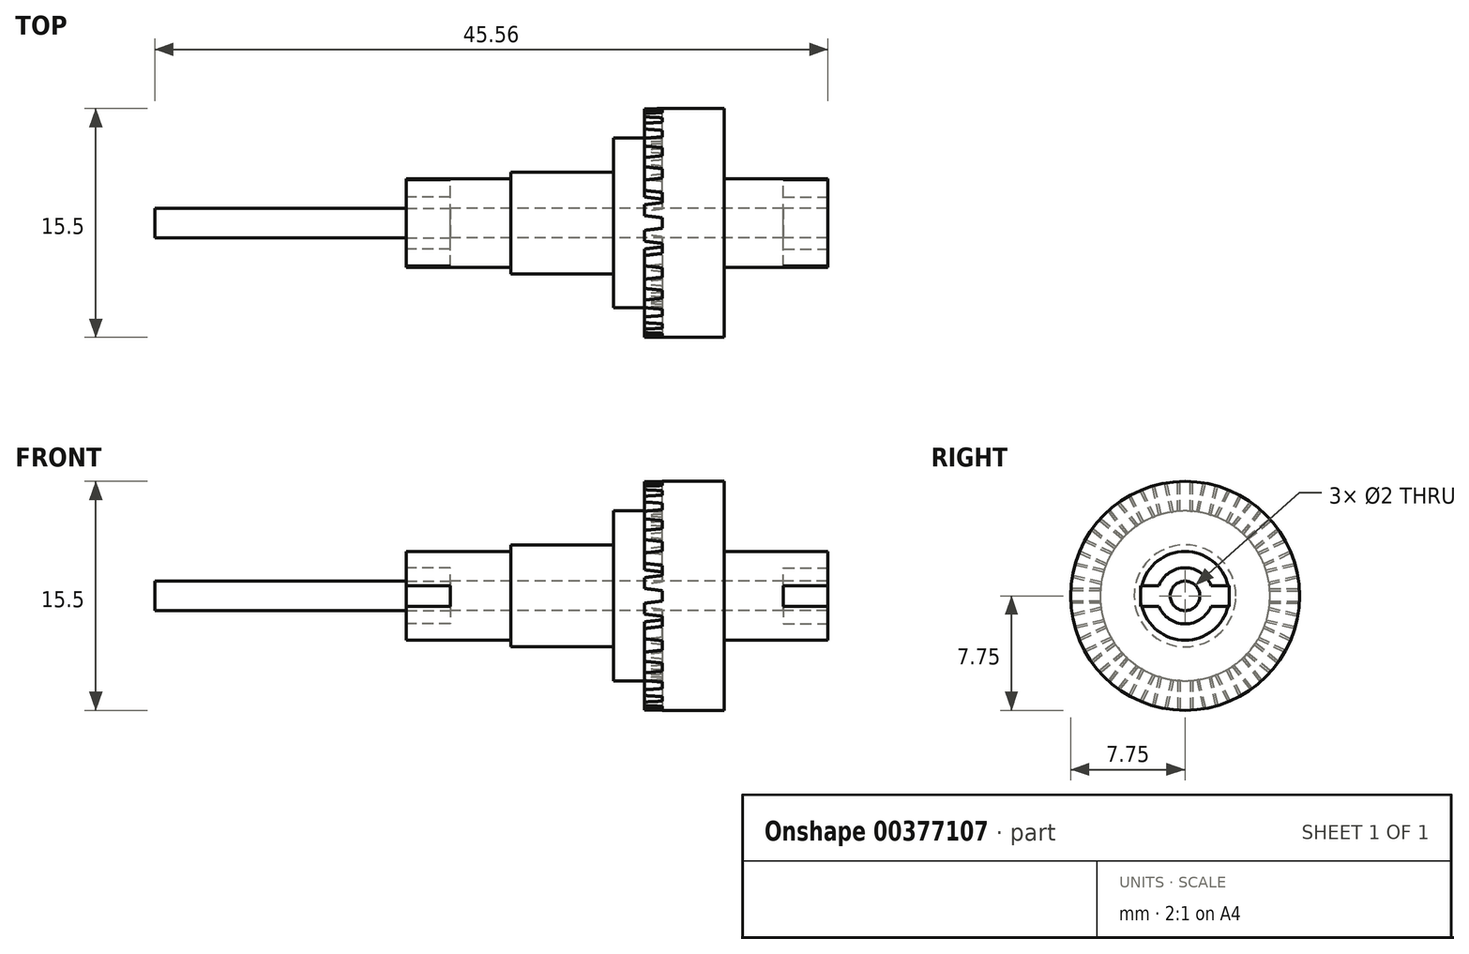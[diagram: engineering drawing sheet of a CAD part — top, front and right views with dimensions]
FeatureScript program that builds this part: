
annotation { "Feature Type Name" : "Feature", "Feature Type Description" : "" }
export const myFeature = defineFeature(function(context is Context, id is Id, definition is map)
    precondition{}
    {
        {
            var Q0;
            Q0=qCreatedBy(makeId("Top.planeOp"),FACE);
            var sketch = newSketch(context, id + "F0", { "sketchPlane" : qUnion([Q0])});
            skLineSegment(sketch, "E0", {"start": v(14.28, 0) * mm, "end": v(-14.28, 0) * mm});
            skLineSegment(sketch, "E1", {"start": v(14.28, 0) * mm, "end": v(14.28, -3) * mm});
            skLineSegment(sketch, "E2", {"start": v(14.28, -3) * mm, "end": v(7.28, -3) * mm});
            skLineSegment(sketch, "E3", {"start": v(7.28, -3) * mm, "end": v(7.28, -7.75) * mm});
            skLineSegment(sketch, "E4", {"start": v(7.28, -7.75) * mm, "end": v(1.88, -7.75) * mm});
            skLineSegment(sketch, "E5", {"start": v(1.88, -7.75) * mm, "end": v(1.88, -5.75) * mm});
            skLineSegment(sketch, "E6", {"start": v(1.88, -5.75) * mm, "end": v(-0.22, -5.75) * mm});
            skLineSegment(sketch, "E7", {"start": v(-0.22, -5.75) * mm, "end": v(-0.22, -3.45) * mm});
            skLineSegment(sketch, "E8", {"start": v(-0.22, -3.45) * mm, "end": v(-7.18, -3.45) * mm});
            skLineSegment(sketch, "E9", {"start": v(-7.18, -3.45) * mm, "end": v(-7.18, -3) * mm});
            skLineSegment(sketch, "E10", {"start": v(-7.18, -3) * mm, "end": v(-14.28, -3) * mm});
            skLineSegment(sketch, "E11", {"start": v(-14.28, -3) * mm, "end": v(-14.28, 0) * mm});
            skLineSegment(sketch, "E12.MirrorCS", {"start": v(-7.18, 3.45) * mm, "end": v(-7.18, 3) * mm, "construction": true});
            skLineSegment(sketch, "E13.MirrorCS", {"start": v(1.88, 5.75) * mm, "end": v(-0.22, 5.75) * mm, "construction": true});
            skLineSegment(sketch, "E14.MirrorCS", {"start": v(1.88, 7.75) * mm, "end": v(1.88, 5.75) * mm, "construction": true});
            skLineSegment(sketch, "E15.MirrorCS", {"start": v(-7.18, 3) * mm, "end": v(-14.28, 3) * mm, "construction": true});
            skLineSegment(sketch, "E16.MirrorCS", {"start": v(14.28, 3) * mm, "end": v(7.28, 3) * mm, "construction": true});
            skLineSegment(sketch, "E17.MirrorCS", {"start": v(7.28, 3) * mm, "end": v(7.28, 7.75) * mm, "construction": true});
            skLineSegment(sketch, "E18.MirrorCS", {"start": v(7.28, 7.75) * mm, "end": v(1.87, 7.75) * mm, "construction": true});
            skLineSegment(sketch, "E19.MirrorCS", {"start": v(-0.22, 5.75) * mm, "end": v(-0.22, 3.45) * mm, "construction": true});
            skLineSegment(sketch, "E20.MirrorCS", {"start": v(-0.22, 3.45) * mm, "end": v(-7.18, 3.45) * mm, "construction": true});
            skLineSegment(sketch, "E21.MirrorCS", {"start": v(-14.28, 3) * mm, "end": v(-14.28, 0) * mm, "construction": true});
            skLineSegment(sketch, "E22.MirrorCS", {"start": v(14.28, 0) * mm, "end": v(14.28, 3) * mm, "construction": true});
            skLineSegment(sketch, "E23", {"start": v(-11.43, 3) * mm, "end": v(-11.43, -3) * mm, "construction": true});
            skSolve(sketch);
        }
        {
            var Q0;
            Q0 = qSketchRegion(id + "F0", true);
            var Q1;
            Q1=sQuery(id+"F0.wireOp",EDGE,"E0");
            revolve(context, id + "F1", {"entities" : qUnion([Q0]), "axis" : qUnion([Q1]), "revolveType" : RevolveType.FULL});
        }
        {
            var Q0;
            Q0=qCreatedBy(makeId("Right.planeOp"),FACE);
            var sketch = newSketch(context, id + "F2", { "sketchPlane" : qUnion([Q0])});
            skLineSegment(sketch, "E24", {"start": v(0, 0) * mm, "end": v(0, 7.75) * mm, "construction": true});
            skSolve(sketch);
        }
        {
            var Q0;
            Q0=qCreatedBy(makeId("Top.planeOp"),FACE);
            var Q1;
            Q1=sQuery(id+"F2.wireOp",VERTEX,"E24.end");
            cPlane(context, id + "F3", {"entities" : qUnion([Q0, Q1]), "cplaneType" : CPlaneType.PLANE_POINT, "offset" : 25 * mm, "width" : 150 * mm, "height" : 150 * mm});
        }
        {
            var Q0;
            Q0=qCreatedBy(id+"F3.planeOp",FACE);
            var sketch = newSketch(context, id + "F4", { "sketchPlane" : qUnion([Q0])});
            skLineSegment(sketch, "E25", {"start": v(1.88, 0.5) * mm, "end": v(1.88, -0.5) * mm});
            skPoint(sketch, "E26", {"position": v(1.88, 0) * mm});
            skLineSegment(sketch, "E27", {"start": v(3.08, 0.35) * mm, "end": v(3.08, -0.35) * mm});
            skPoint(sketch, "E28", {"position": v(3.08, 0) * mm});
            skLineSegment(sketch, "E29", {"start": v(1.88, 0.5) * mm, "end": v(3.08, 0.35) * mm});
            skLineSegment(sketch, "E30", {"start": v(1.88, -0.5) * mm, "end": v(3.08, -0.35) * mm});
            skSolve(sketch);
        }
        {
            var Q0;
            Q0 = qSketchRegion(id + "F4", true);
            var Q1;
            Q1=makeQuery(id+"F1.opRevolve","SWEPT_FACE",FACE,{"disambiguationData":[OSD([sQuery(id+"F0.wireOp",EDGE,"E6")])]});
            extrude(context, id + "F5", {"entities" : qUnion([Q0]), "endBound" : BoundingType.UP_TO_SURFACE, "oppositeDirection" : true, "endBoundEntityFace" : qUnion([Q1]), "depth" : 25 * mm});
        }
        {
            var Q0;
            Q0=makeQuery(id+"F5.opExtrude","SWEPT_BODY",BODY,{"disambiguationData":[OSD([sQuery(id+"F4.wireOp",EDGE,"E25"),sQuery(id+"F4.wireOp",EDGE,"E27"),sQuery(id+"F4.wireOp",EDGE,"E29"),sQuery(id+"F4.wireOp",EDGE,"E30")])]});
            var Q1;
            Q1=makeQuery(id+"F1.opRevolve","SWEPT_EDGE",EDGE,{"disambiguationData":[OSD([sQuery(id+"F0.wireOp",EDGE,"E4"),sQuery(id+"F0.wireOp",EDGE,"E5")])]});
            circularPattern(context, id + "F6", {"operationType" : NewBodyOperationType.REMOVE, "entities" : qUnion([Q0]), "axis" : qUnion([Q1]), "angle" : 360 * degree, "instanceCount" : 28, "equalSpace" : true});
        }
        {
            var Q0;
            Q0=makeQuery(id+"F1.opRevolve","SWEPT_FACE",FACE,{"disambiguationData":[OSD([sQuery(id+"F0.wireOp",EDGE,"E11")])]});
            var sketch = newSketch(context, id + "F7", { "sketchPlane" : qUnion([Q0])});
            skLineSegment(sketch, "E31.bottom", {"start": v(3, 0.7) * mm, "end": v(1.77, 0.7) * mm});
            skLineSegment(sketch, "E31.top", {"start": v(3, -0.7) * mm, "end": v(1.77, -0.7) * mm});
            skLineSegment(sketch, "E31.left", {"start": v(3, 0.7) * mm, "end": v(3, -0.7) * mm});
            skLineSegment(sketch, "E31.right", {"start": v(-3, 0.7) * mm, "end": v(-3, -0.7) * mm});
            skPoint(sketch, "E31.middle", {"position": v(0, 0) * mm});
            skArc(sketch, "E32", {"start": v(-1.77, -0.7) * mm, "mid": v(0, -1.9) * mm, "end": v(1.77, -0.7) * mm});
            skArc(sketch, "E33.trimOffspring", {"start": v(1.77, 0.7) * mm, "mid": v(0, 1.9) * mm, "end": v(-1.77, 0.7) * mm});
            skLineSegment(sketch, "E34.trimOffspring", {"start": v(-1.77, 0.7) * mm, "end": v(-3, 0.7) * mm});
            skLineSegment(sketch, "E35.trimOffspring", {"start": v(-1.77, -0.7) * mm, "end": v(-3, -0.7) * mm});
            skSolve(sketch);
        }
        {
            var Q0;
            Q0 = qSketchRegion(id + "F7", true);
            extrude(context, id + "F8", {"entities" : qUnion([Q0]), "oppositeDirection" : true, "depth" : 3 * mm});
        }
        {
            var Q0;
            Q0=makeQuery(id+"F8.opExtrude","SWEPT_BODY",BODY,{"disambiguationData":[OSD([sQuery(id+"F7.wireOp",EDGE,"E31.bottom"),sQuery(id+"F7.wireOp",EDGE,"E31.top"),sQuery(id+"F7.wireOp",EDGE,"E31.left"),sQuery(id+"F7.wireOp",EDGE,"E31.right"),sQuery(id+"F7.wireOp",EDGE,"E32"),sQuery(id+"F7.wireOp",EDGE,"E33.trimOffspring"),sQuery(id+"F7.wireOp",EDGE,"E34.trimOffspring"),sQuery(id+"F7.wireOp",EDGE,"E35.trimOffspring")])]});
            var Q1;
            Q1=qCreatedBy(makeId("Right.planeOp"),FACE);
            mirror(context, id + "F9", {"entities" : qUnion([Q0]), "mirrorPlane" : qUnion([Q1])});
        }
        {
            var Q0;
            Q0=makeQuery(id+"F8.opExtrude","SWEPT_BODY",BODY,{"disambiguationData":[OSD([sQuery(id+"F7.wireOp",EDGE,"E31.bottom"),sQuery(id+"F7.wireOp",EDGE,"E31.top"),sQuery(id+"F7.wireOp",EDGE,"E31.left"),sQuery(id+"F7.wireOp",EDGE,"E31.right"),sQuery(id+"F7.wireOp",EDGE,"E32"),sQuery(id+"F7.wireOp",EDGE,"E33.trimOffspring"),sQuery(id+"F7.wireOp",EDGE,"E34.trimOffspring"),sQuery(id+"F7.wireOp",EDGE,"E35.trimOffspring")])]});
            var Q1;
            Q1=makeQuery(id+"F9.opPattern","COPY",BODY,{"derivedFrom":makeQuery(id+"F8.opExtrude","SWEPT_BODY",BODY,{"disambiguationData":[OSD([sQuery(id+"F7.wireOp",EDGE,"E31.bottom"),sQuery(id+"F7.wireOp",EDGE,"E31.top"),sQuery(id+"F7.wireOp",EDGE,"E31.left"),sQuery(id+"F7.wireOp",EDGE,"E31.right"),sQuery(id+"F7.wireOp",EDGE,"E32"),sQuery(id+"F7.wireOp",EDGE,"E33.trimOffspring"),sQuery(id+"F7.wireOp",EDGE,"E34.trimOffspring"),sQuery(id+"F7.wireOp",EDGE,"E35.trimOffspring")])]}),"instanceName":"1"});
            var Q2;
            Q2=makeQuery(id+"F1.opRevolve","SWEPT_BODY",BODY,{"disambiguationData":[OSD([sQuery(id+"F0.wireOp",EDGE,"E0"),sQuery(id+"F0.wireOp",EDGE,"E1"),sQuery(id+"F0.wireOp",EDGE,"E2"),sQuery(id+"F0.wireOp",EDGE,"E3"),sQuery(id+"F0.wireOp",EDGE,"E4"),sQuery(id+"F0.wireOp",EDGE,"E5"),sQuery(id+"F0.wireOp",EDGE,"E6"),sQuery(id+"F0.wireOp",EDGE,"E7"),sQuery(id+"F0.wireOp",EDGE,"E8"),sQuery(id+"F0.wireOp",EDGE,"E9"),sQuery(id+"F0.wireOp",EDGE,"E10"),sQuery(id+"F0.wireOp",EDGE,"E11")])]});
            booleanBodies(context, id + "F10", {"operationType" : BooleanOperationType.SUBTRACTION, "tools" : qUnion([Q0, Q1]), "targets" : qUnion([Q2]), "keepTools" : true});
        }
        {
            var Q0;
            Q0=makeQuery(id+"F8.opExtrude","CAP_FACE",FACE,{"disambiguationData":[OSD([sQuery(id+"F7.wireOp",EDGE,"E31.bottom"),sQuery(id+"F7.wireOp",EDGE,"E31.top"),sQuery(id+"F7.wireOp",EDGE,"E31.left"),sQuery(id+"F7.wireOp",EDGE,"E31.right"),sQuery(id+"F7.wireOp",EDGE,"E32"),sQuery(id+"F7.wireOp",EDGE,"E33.trimOffspring"),sQuery(id+"F7.wireOp",EDGE,"E34.trimOffspring"),sQuery(id+"F7.wireOp",EDGE,"E35.trimOffspring")])],"isStart":true});
            var sketch = newSketch(context, id + "F11", { "sketchPlane" : qUnion([Q0])});
            skCircle(sketch, "E36", {"center": v(0, 0) * mm, "radius": 1 * mm});
            skSolve(sketch);
        }
        {
            var Q0;
            Q0 = qSketchRegion(id + "F11", true);
            var Q1;
            Q1=makeQuery(id+"F9.opPattern","COPY",FACE,{"derivedFrom":makeQuery(id+"F8.opExtrude","CAP_FACE",FACE,{"disambiguationData":[OSD([sQuery(id+"F7.wireOp",EDGE,"E31.bottom"),sQuery(id+"F7.wireOp",EDGE,"E31.top"),sQuery(id+"F7.wireOp",EDGE,"E31.left"),sQuery(id+"F7.wireOp",EDGE,"E31.right"),sQuery(id+"F7.wireOp",EDGE,"E32"),sQuery(id+"F7.wireOp",EDGE,"E33.trimOffspring"),sQuery(id+"F7.wireOp",EDGE,"E34.trimOffspring"),sQuery(id+"F7.wireOp",EDGE,"E35.trimOffspring")])],"isStart":true}),"instanceName":"1"});
            extrude(context, id + "F12", {"entities" : qUnion([Q0]), "operationType" : NewBodyOperationType.REMOVE, "endBound" : BoundingType.UP_TO_SURFACE, "oppositeDirection" : true, "endBoundEntityFace" : qUnion([Q1]), "depth" : 25 * mm});
        }
        {
            var Q0;
            Q0=makeQuery(id+"F10.opBoolean","COPY",FACE,{"derivedFrom":makeQuery(id+"F8.opExtrude","CAP_FACE",FACE,{"disambiguationData":[OSD([sQuery(id+"F7.wireOp",EDGE,"E31.bottom"),sQuery(id+"F7.wireOp",EDGE,"E31.top"),sQuery(id+"F7.wireOp",EDGE,"E31.left"),sQuery(id+"F7.wireOp",EDGE,"E31.right"),sQuery(id+"F7.wireOp",EDGE,"E32"),sQuery(id+"F7.wireOp",EDGE,"E33.trimOffspring"),sQuery(id+"F7.wireOp",EDGE,"E34.trimOffspring"),sQuery(id+"F7.wireOp",EDGE,"E35.trimOffspring")])],"isStart":false})});
            var sketch = newSketch(context, id + "F13", { "sketchPlane" : qUnion([Q0])});
            skCircle(sketch, "E37.0", {"center": v(0, 0) * mm, "radius": 1 * mm});
            skSolve(sketch);
        }
        {
            var Q0;
            Q0 = qSketchRegion(id + "F13", true);
            extrude(context, id + "F14", {"entities" : qUnion([Q0]), "depth" : 20 * mm});
        }
    });
